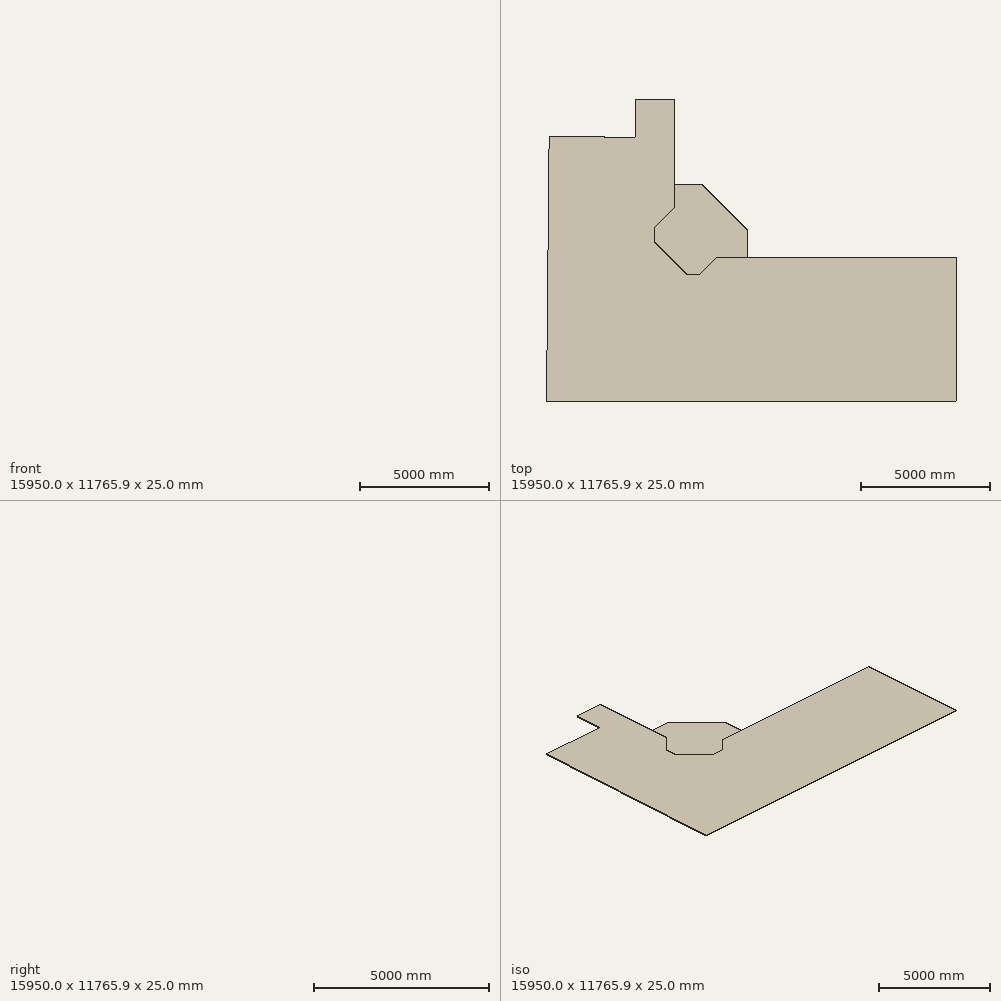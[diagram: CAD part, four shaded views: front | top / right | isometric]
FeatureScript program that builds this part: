
annotation { "Feature Type Name" : "Feature", "Feature Type Description" : "" }
export const myFeature = defineFeature(function(context is Context, id is Id, definition is map)
    precondition{}
    {
        {
            var Q0;
            Q0=qCreatedBy(makeId("Top.planeOp"),FACE);
            var sketch = newSketch(context, id + "F3", { "sketchPlane" : qUnion([Q0])});
            skLineSegment(sketch, "E0", {"start": v(15532.74, 19123.08) * mm, "end": v(15532.74, 19123.08) * mm});
            skLineSegment(sketch, "E1", {"start": v(15532.74, 19123.08) * mm, "end": v(15715.44, 19123.08) * mm});
            skLineSegment(sketch, "E2", {"start": v(15715.44, 19123.08) * mm, "end": v(15715.44, 19123.08) * mm});
            skLineSegment(sketch, "E3", {"start": v(15715.44, -1019.61) * mm, "end": v(15715.44, -1019.61) * mm});
            skLineSegment(sketch, "E4", {"start": v(-234.56, -1019.61) * mm, "end": v(15715.44, -1019.61) * mm});
            skLineSegment(sketch, "E5", {"start": v(-131.8, 9299.88) * mm, "end": v(-234.56, -1019.61) * mm});
            skLineSegment(sketch, "E6", {"start": v(-131.8, 9299.88) * mm, "end": v(3238.04, 9266.32) * mm});
            skLineSegment(sketch, "E7", {"start": v(3238.04, 9266.32) * mm, "end": v(3238.04, 10746.32) * mm});
            skLineSegment(sketch, "E8", {"start": v(3238.04, 10746.32) * mm, "end": v(4748.04, 10746.32) * mm});
            skLineSegment(sketch, "E9", {"start": v(4748.04, 10746.32) * mm, "end": v(4748.04, 6526.32) * mm});
            skLineSegment(sketch, "E10", {"start": v(4748.04, 6526.32) * mm, "end": v(3963.15, 5741.43) * mm});
            skLineSegment(sketch, "E11", {"start": v(3963.15, 5741.43) * mm, "end": v(3963.15, 5181.43) * mm});
            skLineSegment(sketch, "E12", {"start": v(3963.15, 5181.43) * mm, "end": v(5200.59, 3944) * mm});
            skLineSegment(sketch, "E13", {"start": v(4581.87, 4562.71) * mm, "end": v(4982.67, 4963.52) * mm, "construction": true});
            skLineSegment(sketch, "E14.MirrorCS", {"start": v(5760.59, 3944) * mm, "end": v(5200.59, 3944) * mm});
            skLineSegment(sketch, "E15", {"start": v(5760.59, 3944) * mm, "end": v(6396.98, 4580.39) * mm});
            skLineSegment(sketch, "E16", {"start": v(6396.98, 4580.39) * mm, "end": v(15715.44, 4580.39) * mm});
            skLineSegment(sketch, "E17", {"start": v(15715.44, 4580.39) * mm, "end": v(15715.44, -1019.61) * mm});
            skLineSegment(sketch, "E18", {"start": v(4748.04, 7426.32) * mm, "end": v(5808.04, 7426.32) * mm});
            skLineSegment(sketch, "E19", {"start": v(5808.04, 7426.32) * mm, "end": v(7589.95, 5644.4) * mm});
            skLineSegment(sketch, "E20", {"start": v(7589.95, 5644.4) * mm, "end": v(7589.95, 4562.71) * mm});
            skSolve(sketch);
        }
        {
            var Q0;
            Q0=sQuery(id+"F3.wireOp",EDGE,"E17");
            var Q1;
            Q1=sQuery(id+"F3.wireOp",EDGE,"E16");
            var Q2;
            Q2=sQuery(id+"F3.wireOp",EDGE,"E5");
            var Q3;
            Q3=sQuery(id+"F3.wireOp",EDGE,"E4");
            var Q4;
            Q4=sQuery(id+"F3.wireOp",EDGE,"E12");
            var Q5;
            Q5=sQuery(id+"F3.wireOp",EDGE,"E8");
            var Q6;
            Q6=sQuery(id+"F3.wireOp",EDGE,"E9");
            var Q7;
            Q7=sQuery(id+"F3.wireOp",EDGE,"E6");
            var Q8;
            Q8=sQuery(id+"F3.wireOp",EDGE,"E15");
            var Q9;
            Q9=sQuery(id+"F3.wireOp",EDGE,"E7");
            var Q10;
            Q10=sQuery(id+"F3.wireOp",EDGE,"E11");
            var Q11;
            Q11=sQuery(id+"F3.wireOp",EDGE,"E14.MirrorCS");
            var Q12;
            Q12=sQuery(id+"F3.wireOp",EDGE,"E10");
            extrude(context, id + "F0", {"bodyType" : ToolBodyType.SURFACE, "surfaceEntities" : qUnion([Q0, Q1, Q2, Q3, Q4, Q5, Q6, Q7, Q8, Q9, Q10, Q11, Q12]), "offsetDistance" : 25 * mm, "depth" : 2000 * mm});
        }
        {
            var Q0;
            Q0=makeQuery(id+"F3.imprint","IMPRINT",FACE,{"disambiguationData":[TD([[makeQuery(id+"F3.imprint","IMPRINT",EDGE,{"derivedFrom":sQuery(id+"F3.wireOp",EDGE,"E4")}),1.0]])]});
            extrude(context, id + "F1", {"entities" : qUnion([Q0]), "depth" : 25 * mm, "offsetDistance" : 25 * mm});
        }
        {
            var Q0;
            {var subQ0=sQuery(id+"F3.wireOp",EDGE,"E10");Q0=makeQuery(id+"F3.imprint","IMPRINT",FACE,{"disambiguationData":[TD([[makeQuery(id+"F3.imprint","IMPRINT",EDGE,{"derivedFrom":subQ0}),1.0]])]});}
            extrude(context, id + "F2", {"entities" : qUnion([Q0]), "depth" : 25 * mm, "offsetDistance" : 25 * mm});
        }
    });
